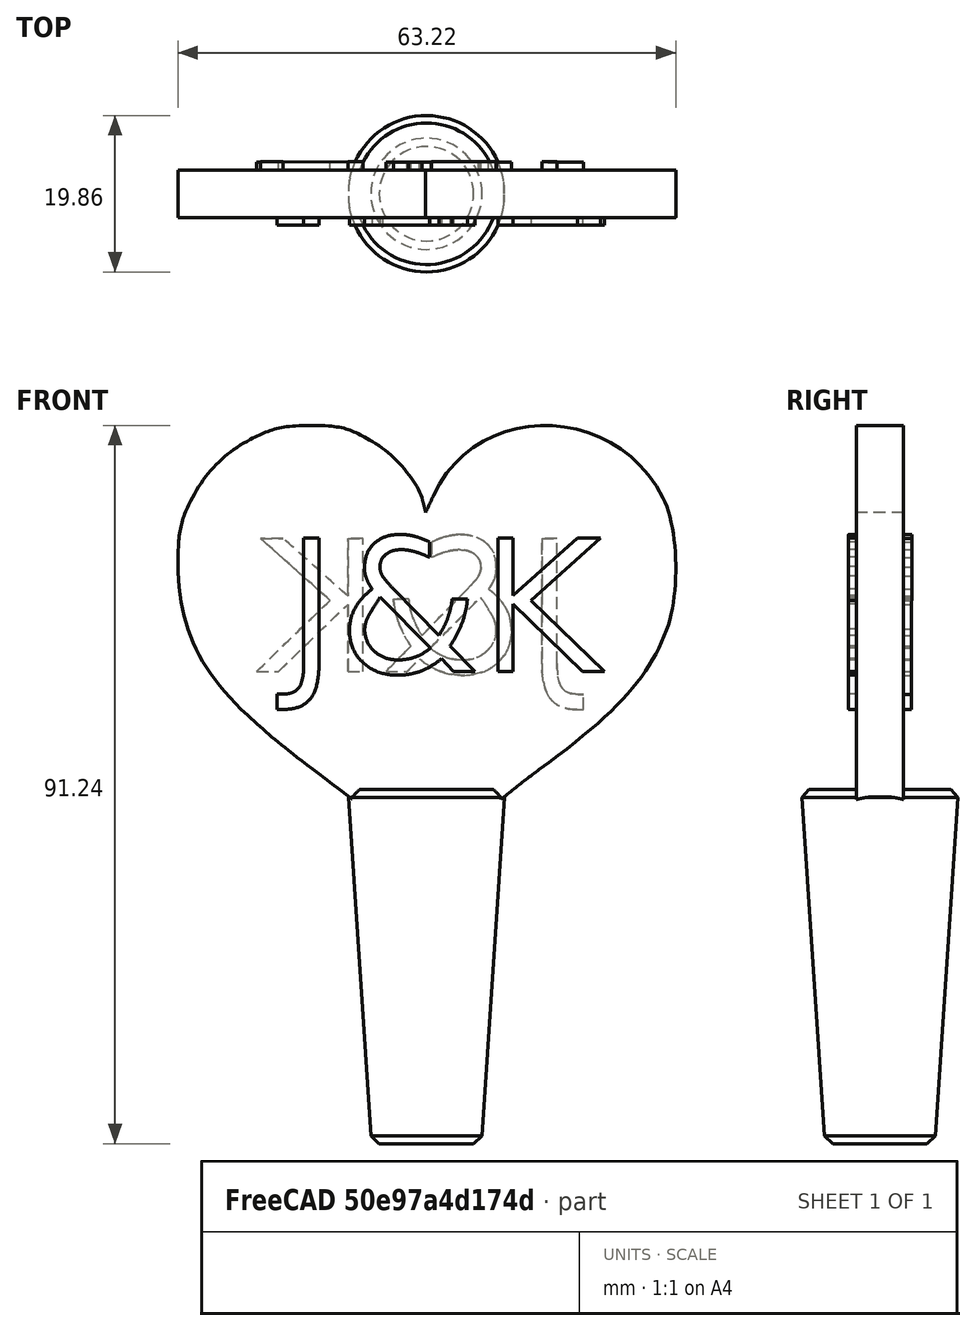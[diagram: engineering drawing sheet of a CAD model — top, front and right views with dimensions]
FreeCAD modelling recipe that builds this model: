
FCSTD DOCUMENT  (FreeCAD 0.14R3702 (Git))
Label: jk-wine-stopper
License: CC-BY 3.0
LicenseURL: http://creativecommons.org/licenses/by/3.0/
objects: Part::Extrusion×3, Part::Part2DObjectPython×2, Part::Cone×1, Part::Feature×1, Part::FeaturePython×1, Part::Chamfer×1, Part::MultiFuse×1
note: 10 computed .brp shape members not serialized (recipe doc carries the construction recipe); baked Part::Feature solids carry a one-line shape summary decoded from their .brp

FEATURE [Part::Cone] Cone
  Angle = 360
  Height = 45
  Placement = pos=(0,0,-6) rot=(0,0,1;0rad)
  Radius1 = 7
  Radius2 = 10
FEATURE [Part::Part2DObjectPython] ShapeString  # Draft 2D object (typed FeaturePython)
  FontFile = <path>
  Size = 18
  String = J&K
  Tracking = 0
FEATURE [Part::Extrusion] Extrude  label="J&K extrude"
  Base = -> ShapeString
  Dir = (0,0,4)
  Placement = pos=(-18,0,54) rot=(1,0,0;1.5708rad)
  Solid = true
FEATURE [Part::Feature] path2417001  label="heart-svg-path"
  shape: bbox 180.8 x 162.8 x 2e-07 mm, 1 faces, 0 solids (baked)
FEATURE [Part::FeaturePython] Scale  # Draft clone (typed FeaturePython)
  Objects = -> [path2417001]
  Placement = pos=(0,0,50) rot=(0,0,1;0rad)
  Scale = (0.35,0.35,0.2)
FEATURE [Part::Extrusion] Extrude002  label="heart-extrude"
  Base = -> Scale
  Dir = (0,0,6)
  Placement = pos=(-31.8,53,86) rot=(1,0,0;1.5708rad)
  Solid = true
FEATURE [Part::Part2DObjectPython] ShapeString001  # Draft 2D object (typed FeaturePython)
  FontFile = <path>
  Size = 18
  String = J&K
  Tracking = 0
FEATURE [Part::Extrusion] Extrude003  label="J&K extrude other side"
  Base = -> ShapeString001
  Dir = (0,0,4)
  Placement = pos=(19,0,54) rot=(0,0.708557,0.705653;3.14159rad)
  Solid = true
FEATURE [Part::Chamfer] Chamfer
  Base = -> Cone
  Edges = 2 edges r=1: [Edge1,Edge3]
FEATURE [Part::MultiFuse] Fusion
  Shapes = -> [Extrude,Extrude003,Chamfer,Extrude002]
note: 2 file-system paths scrubbed to <path> (originals preserved in the JSON sidecar)
